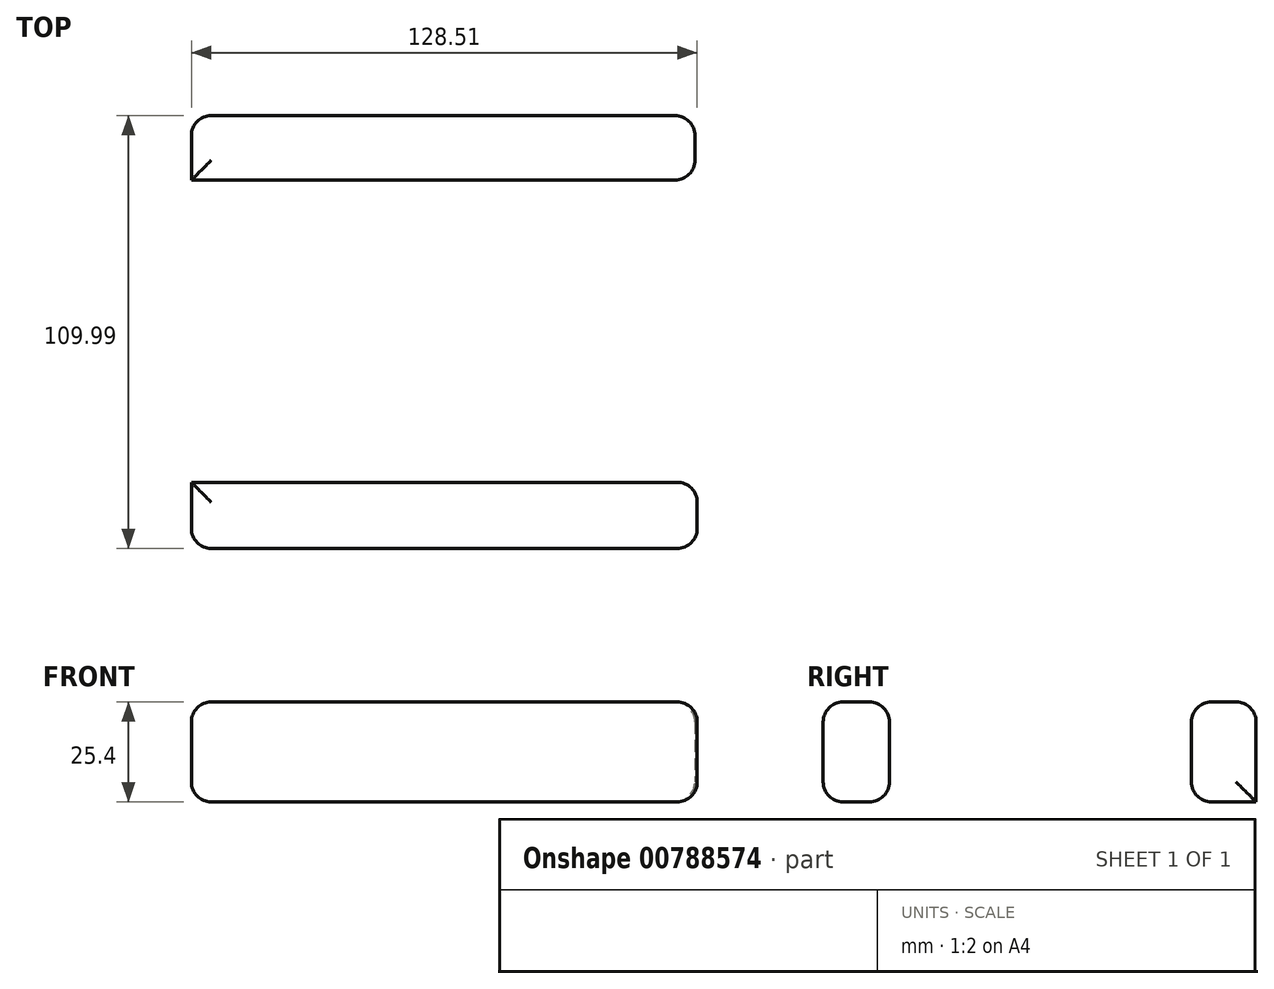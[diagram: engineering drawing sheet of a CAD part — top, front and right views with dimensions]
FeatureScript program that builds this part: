
annotation { "Feature Type Name" : "Feature", "Feature Type Description" : "" }
export const myFeature = defineFeature(function(context is Context, id is Id, definition is map)
    precondition{}
    {
        {
            var Q0;
            Q0=qCreatedBy(makeId("Top.planeOp"),FACE);
            var sketch = newSketch(context, id + "F0", { "sketchPlane" : qUnion([Q0])});
            skLineSegment(sketch, "E0.bottom", {"start": v(-63.11, 53.94) * mm, "end": v(64.83, 53.94) * mm});
            skLineSegment(sketch, "E0.top", {"start": v(-63.11, 37.52) * mm, "end": v(64.83, 37.52) * mm});
            skLineSegment(sketch, "E0.left", {"start": v(-63.11, 53.94) * mm, "end": v(-63.11, 37.52) * mm});
            skLineSegment(sketch, "E0.right", {"start": v(64.83, 53.94) * mm, "end": v(64.83, 37.52) * mm});
            skLineSegment(sketch, "E1.bottom", {"start": v(-63.11, 37.52) * mm, "end": v(-32.94, 37.52) * mm});
            skLineSegment(sketch, "E1.top", {"start": v(-63.11, -39.24) * mm, "end": v(-32.94, -39.24) * mm});
            skLineSegment(sketch, "E1.left", {"start": v(-63.11, 37.52) * mm, "end": v(-63.11, -39.24) * mm});
            skLineSegment(sketch, "E1.right", {"start": v(-32.94, 37.52) * mm, "end": v(-32.94, -39.24) * mm});
            skLineSegment(sketch, "E2.bottom", {"start": v(-63.11, -39.24) * mm, "end": v(65.4, -39.24) * mm});
            skLineSegment(sketch, "E2.top", {"start": v(-63.11, -56.05) * mm, "end": v(65.4, -56.05) * mm});
            skLineSegment(sketch, "E2.left", {"start": v(-63.11, -39.24) * mm, "end": v(-63.11, -56.05) * mm});
            skLineSegment(sketch, "E2.right", {"start": v(65.4, -39.24) * mm, "end": v(65.4, -56.05) * mm});
            skSolve(sketch);
        }
        {
            var Q0;
            Q0=makeQuery(id+"F0.imprint","IMPRINT",FACE,{"disambiguationData":[TD([[makeQuery(id+"F0.imprint","IMPRINT",EDGE,{"derivedFrom":sQuery(id+"F0.wireOp",EDGE,"E1.bottom")}),-1.0]])]});
            var Q1;
            Q1=makeQuery(id+"F0.imprint","IMPRINT",FACE,{"disambiguationData":[TD([[makeQuery(id+"F0.imprint","IMPRINT",EDGE,{"derivedFrom":sQuery(id+"F0.wireOp",EDGE,"E2.top")}),1.0]])]});
            var Q2;
            Q2=makeQuery(id+"F0.imprint","IMPRINT",FACE,{"disambiguationData":[TD([[makeQuery(id+"F0.imprint","IMPRINT",EDGE,{"derivedFrom":sQuery(id+"F0.wireOp",EDGE,"E0.bottom")}),-1.0]])]});
            extrude(context, id + "F1", {"entities" : qUnion([Q0, Q1, Q2]), "depth" : 25.4 * mm, "offsetDistance" : 25.4 * mm});
        }
        {
            var Q0;
            Q0=makeQuery(id+"F1.opExtrude","CAP_EDGE",EDGE,{"disambiguationData":[OSD([sQuery(id+"F0.wireOp",EDGE,"E0.top")])],"isStart":false});
            var Q1;
            Q1=makeQuery(id+"F1.opExtrude","CAP_EDGE",EDGE,{"disambiguationData":[OSD([sQuery(id+"F0.wireOp",EDGE,"E1.right")])],"isStart":false});
            var Q2;
            Q2=makeQuery(id+"F1.opExtrude","CAP_EDGE",EDGE,{"disambiguationData":[OSD([sQuery(id+"F0.wireOp",EDGE,"E2.bottom")])],"isStart":false});
            var Q3;
            Q3=makeQuery(id+"F1.opExtrude","CAP_EDGE",EDGE,{"disambiguationData":[OSD([sQuery(id+"F0.wireOp",EDGE,"E2.right")])],"isStart":false});
            var Q4;
            Q4=makeQuery(id+"F1.opExtrude","CAP_EDGE",EDGE,{"disambiguationData":[OSD([sQuery(id+"F0.wireOp",EDGE,"E0.right")])],"isStart":false});
            var Q5;
            Q5=makeQuery(id+"F1.opExtrude","CAP_EDGE",EDGE,{"disambiguationData":[OSD([sQuery(id+"F0.wireOp",EDGE,"E2.top")])],"isStart":false});
            var Q6;
            Q6=makeQuery(id+"F1.opExtrude","SWEPT_EDGE",EDGE,{"disambiguationData":[OSD([sQuery(id+"F0.wireOp",EDGE,"E2.top"),sQuery(id+"F0.wireOp",EDGE,"E2.right")])]});
            var Q7;
            Q7=makeQuery(id+"F1.opExtrude","SWEPT_EDGE",EDGE,{"disambiguationData":[OSD([sQuery(id+"F0.wireOp",EDGE,"E2.bottom"),sQuery(id+"F0.wireOp",EDGE,"E2.right")])]});
            var Q8;
            Q8=makeQuery(id+"F1.opExtrude","SWEPT_EDGE",EDGE,{"disambiguationData":[OSD([sQuery(id+"F0.wireOp",EDGE,"E2.top"),sQuery(id+"F0.wireOp",EDGE,"E2.left")])]});
            var Q9;
            Q9=makeQuery(id+"F1.opExtrude","CAP_EDGE",EDGE,{"disambiguationData":[OSD([sQuery(id+"F0.wireOp",EDGE,"E0.left"),sQuery(id+"F0.wireOp",EDGE,"E1.left"),sQuery(id+"F0.wireOp",EDGE,"E2.left")])],"isStart":false});
            var Q10;
            Q10=makeQuery(id+"F1.opExtrude","CAP_EDGE",EDGE,{"disambiguationData":[OSD([sQuery(id+"F0.wireOp",EDGE,"E0.bottom")])],"isStart":false});
            var Q11;
            Q11=makeQuery(id+"F1.opExtrude","SWEPT_EDGE",EDGE,{"disambiguationData":[OSD([sQuery(id+"F0.wireOp",EDGE,"E0.top"),sQuery(id+"F0.wireOp",EDGE,"E0.right")])]});
            var Q12;
            Q12=makeQuery(id+"F1.opExtrude","SWEPT_EDGE",EDGE,{"disambiguationData":[OSD([sQuery(id+"F0.wireOp",EDGE,"E0.bottom"),sQuery(id+"F0.wireOp",EDGE,"E0.right")])]});
            var Q13;
            Q13=makeQuery(id+"F1.opExtrude","SWEPT_EDGE",EDGE,{"disambiguationData":[OSD([sQuery(id+"F0.wireOp",EDGE,"E0.bottom"),sQuery(id+"F0.wireOp",EDGE,"E0.left")])]});
            var Q14;
            Q14=makeQuery(id+"F1.opExtrude","CAP_EDGE",EDGE,{"disambiguationData":[OSD([sQuery(id+"F0.wireOp",EDGE,"E0.left"),sQuery(id+"F0.wireOp",EDGE,"E1.left"),sQuery(id+"F0.wireOp",EDGE,"E2.left")])],"isStart":true});
            var Q15;
            Q15=makeQuery(id+"F1.opExtrude","CAP_EDGE",EDGE,{"disambiguationData":[OSD([sQuery(id+"F0.wireOp",EDGE,"E2.top")])],"isStart":true});
            var Q16;
            Q16=makeQuery(id+"F1.opExtrude","CAP_EDGE",EDGE,{"disambiguationData":[OSD([sQuery(id+"F0.wireOp",EDGE,"E0.top")])],"isStart":true});
            var Q17;
            Q17=makeQuery(id+"F1.opExtrude","CAP_EDGE",EDGE,{"disambiguationData":[OSD([sQuery(id+"F0.wireOp",EDGE,"E1.right")])],"isStart":true});
            var Q18;
            Q18=makeQuery(id+"F1.opExtrude","CAP_EDGE",EDGE,{"disambiguationData":[OSD([sQuery(id+"F0.wireOp",EDGE,"E2.bottom")])],"isStart":true});
            var Q19;
            Q19=makeQuery(id+"F1.opExtrude","CAP_EDGE",EDGE,{"disambiguationData":[OSD([sQuery(id+"F0.wireOp",EDGE,"E2.right")])],"isStart":true});
            var Q20;
            Q20=makeQuery(id+"F1.opExtrude","CAP_EDGE",EDGE,{"disambiguationData":[OSD([sQuery(id+"F0.wireOp",EDGE,"E0.right")])],"isStart":true});
            fillet(context, id + "F2", {"entities" : qUnion([Q0, Q1, Q2, Q3, Q4, Q5, Q6, Q7, Q8, Q9, Q10, Q11, Q12, Q13, Q14, Q15, Q16, Q17, Q18, Q19, Q20]), "radius" : 5.08 * mm, "tangentPropagation" : true, "allowEdgeOverflow" : false});
        }
    });
